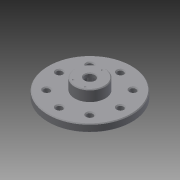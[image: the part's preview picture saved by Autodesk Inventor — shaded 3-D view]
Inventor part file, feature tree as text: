
AUTODESK INVENTOR PART (.ipt)
format: ipt  version: 2016 (Build 200138000, 138)  size: 482,816 bytes
history: native  units: in
note: dims shown in document units (in); Inventor stores cm internally (conversion verified against a paired STEP export)
features: other x3, hole x2, sketch x2, imported_body x1
ambient origin geometry x8: Origin, YZ Plane, XZ Plane, XY Plane, X Axis, Y Axis, Z Axis, Center Point
bodies: Solid1 (feature_tree)
feature tree (8):
  other  "HN07-N1011"
  hole  "Hole1"  [1 undecoded]
  hole  "Hole2"  [1 undecoded]
  imported_body  "Base1"
  sketch  "Sketch2"  dims[d0=0.2244in]
  sketch  "Sketch3"  dims[d1=0.2244in d2=0.2362in d3=0.1575in d4=0.0787in d5=90.0deg d6=0.065in d7=0.0in d8=0.2244in d9=0.2362in d10=0.1575in d11=0.0787in d12=90.0deg d13=0.315in d14=0.8108in]
  other  "Composite1"
  other  "Srf1"
note: 2 required parameter values undecoded (feature->parameter linkage not recoverable at this tier; creation-order binding heuristic only, values carry confidence <= 0.55)
